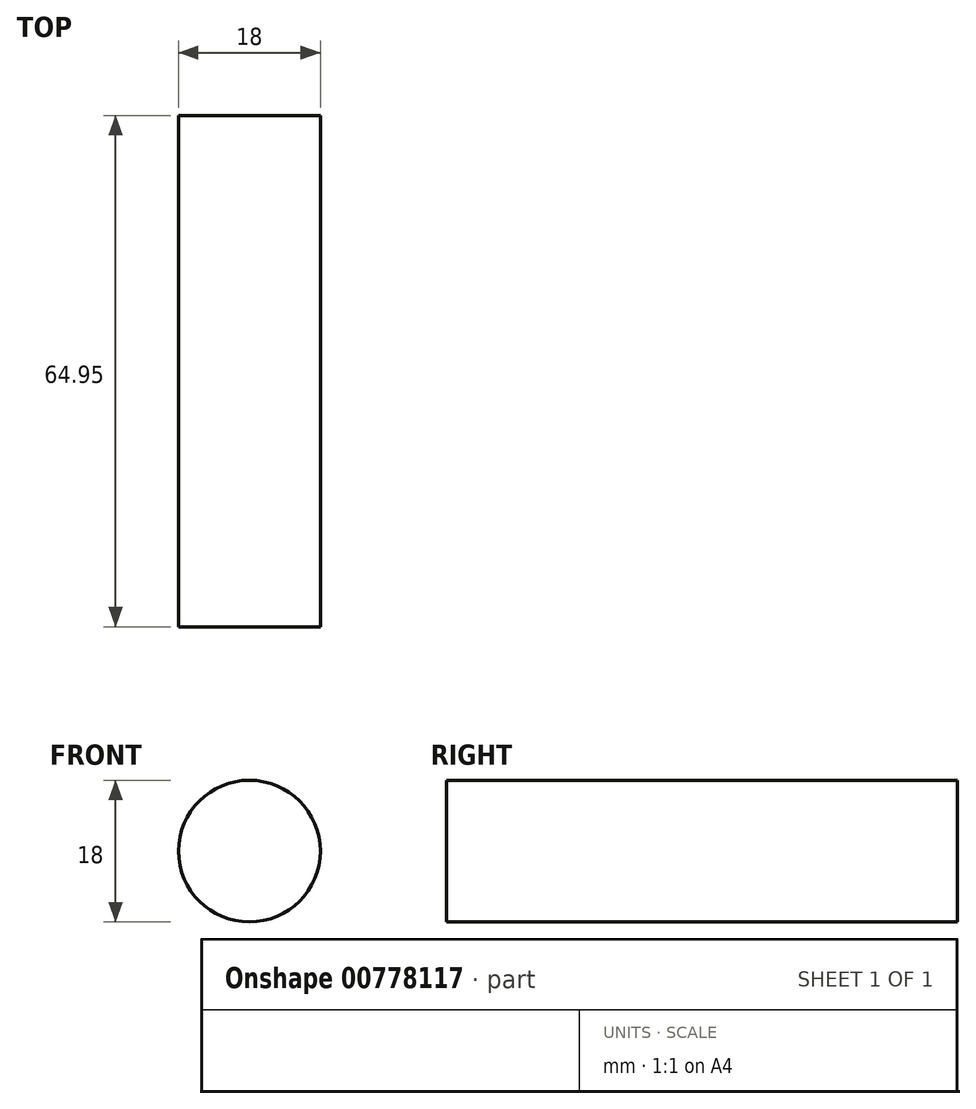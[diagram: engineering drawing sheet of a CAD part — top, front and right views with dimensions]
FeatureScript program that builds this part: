
annotation { "Feature Type Name" : "Feature", "Feature Type Description" : "" }
export const myFeature = defineFeature(function(context is Context, id is Id, definition is map)
    precondition{}
    {
        {
            var Q0;
            Q0=qCreatedBy(makeId("Front.planeOp"),FACE);
            var sketch = newSketch(context, id + "F0", { "sketchPlane" : qUnion([Q0])});
            skCircle(sketch, "E0", {"center": v(0, 0) * mm, "radius": 9 * mm});
            skSolve(sketch);
        }
        {
            var Q0;
            Q0 = qSketchRegion(id + "F0", true);
            extrude(context, id + "F1", {"entities" : qUnion([Q0]), "depth" : 64.95 * mm, "offsetDistance" : 25 * mm});
        }
    });
